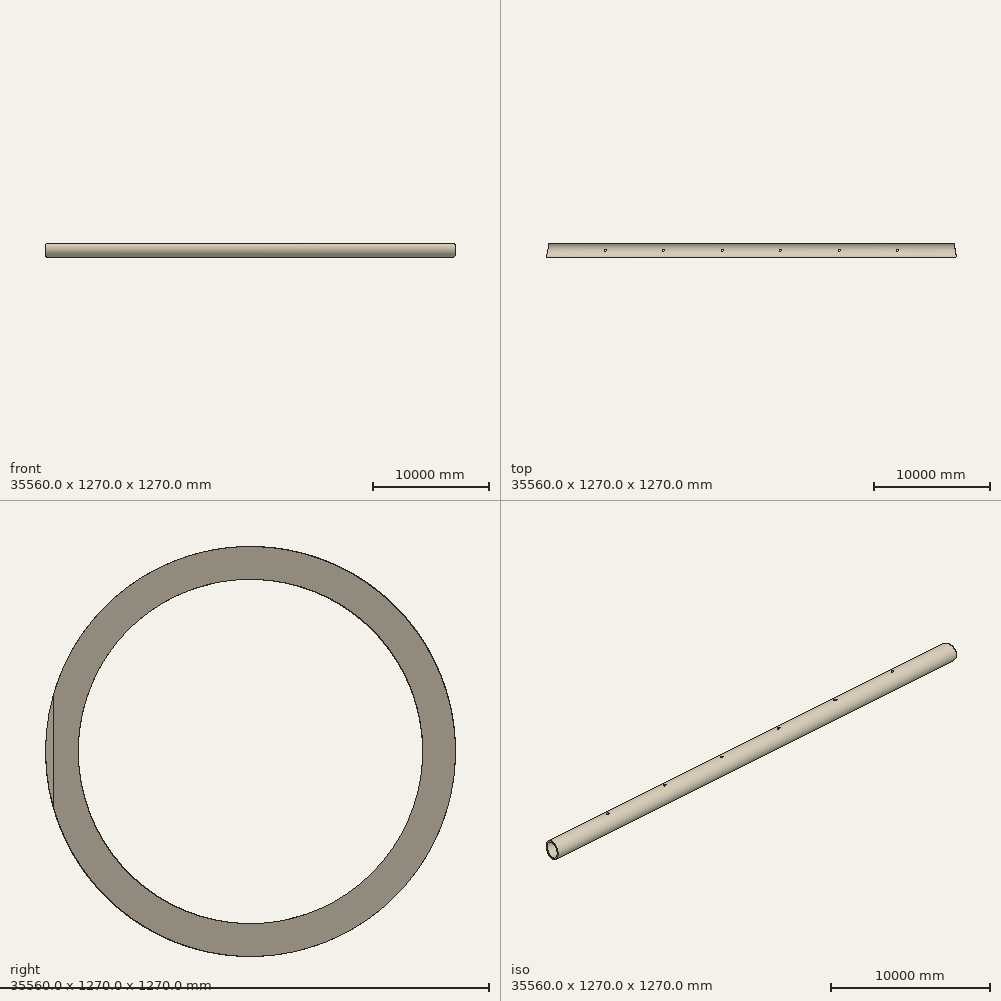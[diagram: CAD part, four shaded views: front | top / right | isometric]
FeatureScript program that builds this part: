
annotation { "Feature Type Name" : "Feature", "Feature Type Description" : "" }
export const myFeature = defineFeature(function(context is Context, id is Id, definition is map)
    precondition{}
    {
        {
            var Q0;
            Q0=qCreatedBy(makeId("Right.planeOp"),FACE);
            var sketch = newSketch(context, id + "F0", { "sketchPlane" : qUnion([Q0])});
            skCircle(sketch, "E0", {"center": v(0, 0) * mm, "radius": 533.4 * mm});
            skCircle(sketch, "E1", {"center": v(0, 0) * mm, "radius": 635 * mm});
            skSolve(sketch);
        }
        {
            var Q0;
            Q0=makeQuery(id+"F0.imprint","IMPRINT",FACE,{"disambiguationData":[TD([[makeQuery(id+"F0.imprint","IMPRINT",EDGE,{"derivedFrom":sQuery(id+"F0.wireOp",EDGE,"E0")}),-1.0]])]});
            extrude(context, id + "F1", {"entities" : qUnion([Q0]), "endBound" : BoundingType.SYMMETRIC, "depth" : 35560 * mm, "offsetDistance" : 25.4 * mm});
        }
        {
            var Q0;
            Q0=qCreatedBy(makeId("Top.planeOp"),FACE);
            var sketch = newSketch(context, id + "F2", { "sketchPlane" : qUnion([Q0])});
            skCircle(sketch, "E2", {"center": v(-12700, 0) * mm, "radius": 101.6 * mm});
            skCircle(sketch, "E3", {"center": v(-7620, 0) * mm, "radius": 101.6 * mm});
            skCircle(sketch, "E4", {"center": v(-2540, 0) * mm, "radius": 101.6 * mm});
            skCircle(sketch, "E5", {"center": v(2540, 0) * mm, "radius": 101.6 * mm});
            skCircle(sketch, "E6", {"center": v(7620, 0) * mm, "radius": 101.6 * mm});
            skCircle(sketch, "E7", {"center": v(12700, 0) * mm, "radius": 101.6 * mm});
            skSolve(sketch);
        }
        {
            var Q0;
            Q0 = qSketchRegion(id + "F2", true);
            extrude(context, id + "F3", {"entities" : qUnion([Q0]), "operationType" : NewBodyOperationType.REMOVE, "endBound" : BoundingType.SYMMETRIC, "oppositeDirection" : true, "depth" : 1524 * mm, "offsetDistance" : 25.4 * mm});
        }
        {
            var Q0;
            Q0=qCreatedBy(makeId("Top.planeOp"),FACE);
            var sketch = newSketch(context, id + "F4", { "sketchPlane" : qUnion([Q0])});
            skLineSegment(sketch, "E8", {"start": v(-17780, 0) * mm, "end": v(-17780, -635) * mm});
            skLineSegment(sketch, "E9", {"start": v(-17780, -635) * mm, "end": v(-17515.76, 863.57) * mm});
            skLineSegment(sketch, "E10", {"start": v(-17515.76, 863.57) * mm, "end": v(-17780, 863.57) * mm});
            skLineSegment(sketch, "E11", {"start": v(-17780, 863.57) * mm, "end": v(-17780, 0) * mm});
            skLineSegment(sketch, "E12", {"start": v(17784.35, 0) * mm, "end": v(17784.35, -635) * mm});
            skLineSegment(sketch, "E13", {"start": v(17784.35, -635) * mm, "end": v(17508.28, 930.68) * mm});
            skLineSegment(sketch, "E14", {"start": v(17508.28, 930.68) * mm, "end": v(18053.08, 930.68) * mm});
            skLineSegment(sketch, "E15", {"start": v(18053.08, 930.68) * mm, "end": v(17784.35, 0) * mm});
            skSolve(sketch);
        }
        {
            var Q0;
            Q0 = qSketchRegion(id + "F4", true);
            extrude(context, id + "F5", {"entities" : qUnion([Q0]), "operationType" : NewBodyOperationType.REMOVE, "endBound" : BoundingType.SYMMETRIC, "oppositeDirection" : true, "depth" : 1524 * mm, "offsetDistance" : 25.4 * mm});
        }
    });
